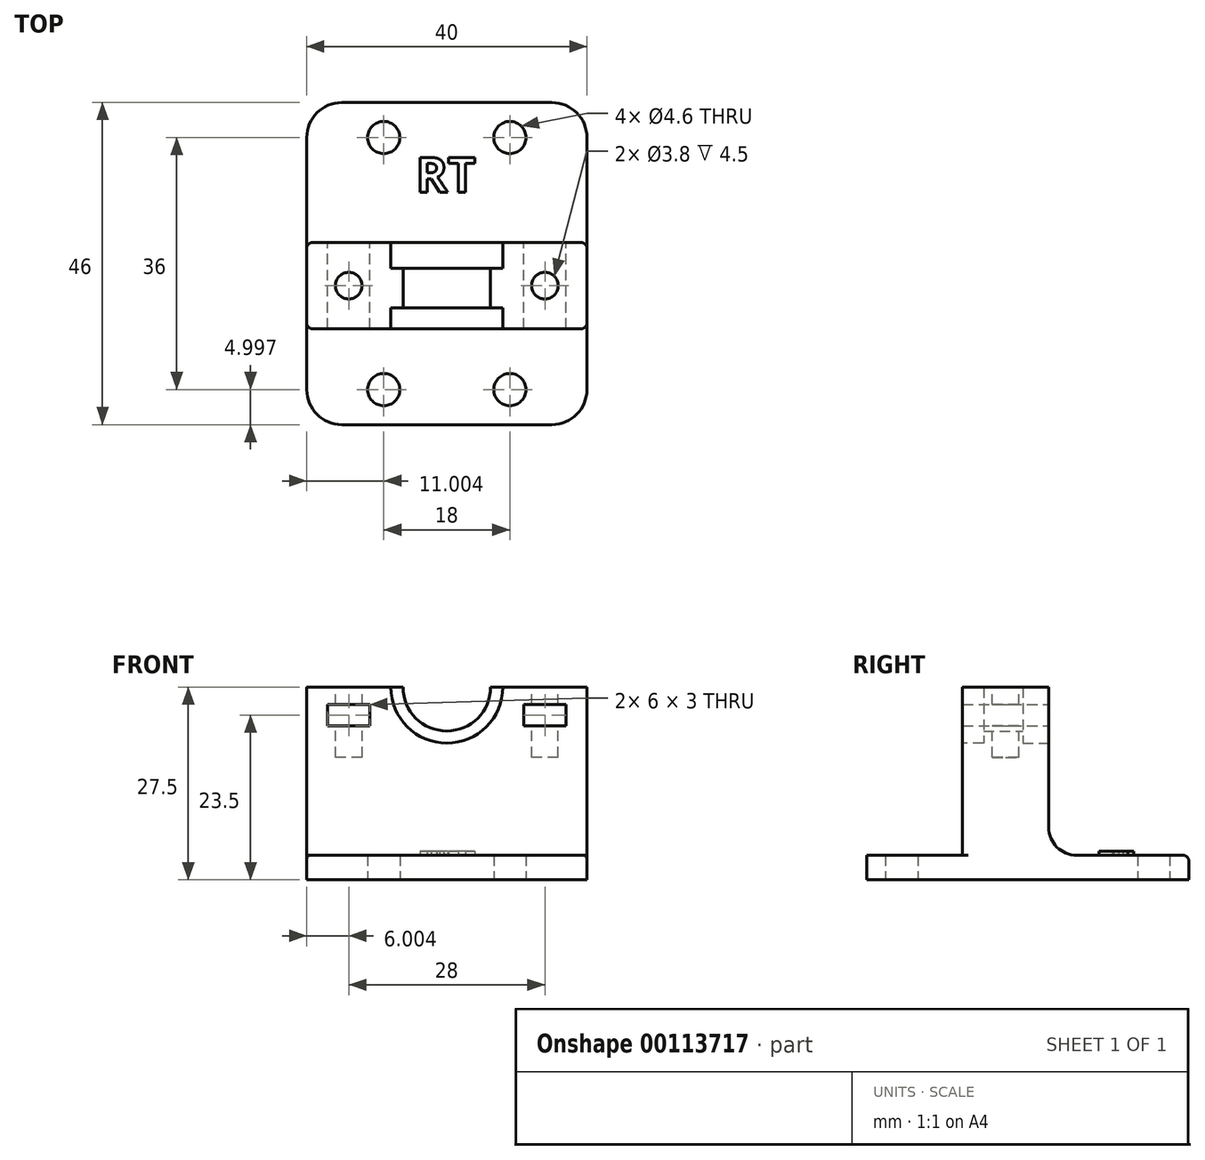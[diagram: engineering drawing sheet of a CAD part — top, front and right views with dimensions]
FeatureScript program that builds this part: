
annotation { "Feature Type Name" : "Feature", "Feature Type Description" : "" }
export const myFeature = defineFeature(function(context is Context, id is Id, definition is map)
    precondition{}
    {
        {
            var Q0;
            Q0=qCreatedBy(makeId("Top.planeOp"),FACE);
            var sketch = newSketch(context, id + "F0", { "sketchPlane" : qUnion([Q0])});
            skLineSegment(sketch, "E0.bottom", {"start": v(-24.7, 19.54) * mm, "end": v(15.3, 19.54) * mm});
            skLineSegment(sketch, "E0.top", {"start": v(-24.7, -26.46) * mm, "end": v(15.3, -26.46) * mm});
            skLineSegment(sketch, "E0.left", {"start": v(-24.7, 19.54) * mm, "end": v(-24.7, -26.46) * mm});
            skLineSegment(sketch, "E0.right", {"start": v(15.3, 19.54) * mm, "end": v(15.3, -26.46) * mm});
            skCircle(sketch, "E1", {"center": v(-13.7, 14.54) * mm, "radius": 2.3 * mm});
            skCircle(sketch, "E2.0.1.0", {"center": v(-13.7, -21.46) * mm, "radius": 2.3 * mm});
            skCircle(sketch, "E2.1.0.0", {"center": v(4.3, 14.54) * mm, "radius": 2.3 * mm});
            skCircle(sketch, "E2.1.1.0", {"center": v(4.3, -21.46) * mm, "radius": 2.3 * mm});
            skLineSegment(sketch, "E2.direction1", {"start": v(-13.7, 14.54) * mm, "end": v(4.3, 14.54) * mm, "construction": true});
            skLineSegment(sketch, "E2.direction2", {"start": v(-13.7, 14.54) * mm, "end": v(-13.7, -21.46) * mm, "construction": true});
            skSolve(sketch);
        }
        {
            var Q0;
            Q0=makeQuery(id+"F0.imprint","IMPRINT",FACE,{"disambiguationData":[TD([[makeQuery(id+"F0.imprint","IMPRINT",EDGE,{"derivedFrom":sQuery(id+"F0.wireOp",EDGE,"E0.bottom")}),-1.0]])]});
            extrude(context, id + "F1", {"entities" : qUnion([Q0]), "depth" : 3.5 * mm});
        }
        {
            var Q0;
            Q0=makeQuery(id+"F1.opExtrude","CAP_FACE",FACE,{"disambiguationData":[OSD([sQuery(id+"F0.wireOp",EDGE,"E0.bottom"),sQuery(id+"F0.wireOp",EDGE,"E0.top"),sQuery(id+"F0.wireOp",EDGE,"E0.left"),sQuery(id+"F0.wireOp",EDGE,"E0.right"),sQuery(id+"F0.wireOp",EDGE,"E1"),sQuery(id+"F0.wireOp",EDGE,"E2.0.1.0"),sQuery(id+"F0.wireOp",EDGE,"E2.1.0.0"),sQuery(id+"F0.wireOp",EDGE,"E2.1.1.0")])],"isStart":false});
            var sketch = newSketch(context, id + "F2", { "sketchPlane" : qUnion([Q0])});
            skLineSegment(sketch, "E3.bottom", {"start": v(-24.7, -0.46) * mm, "end": v(15.3, -0.46) * mm});
            skLineSegment(sketch, "E3.top", {"start": v(-24.7, -12.76) * mm, "end": v(15.3, -12.76) * mm});
            skLineSegment(sketch, "E3.left", {"start": v(-24.7, -0.46) * mm, "end": v(-24.7, -12.76) * mm});
            skLineSegment(sketch, "E3.right", {"start": v(15.3, -0.46) * mm, "end": v(15.3, -12.76) * mm});
            skSolve(sketch);
        }
        {
            var Q0;
            Q0=makeQuery(id+"F2.imprint","IMPRINT",FACE,{"disambiguationData":[TD([[makeQuery(id+"F2.imprint","IMPRINT",EDGE,{"derivedFrom":sQuery(id+"F2.wireOp",EDGE,"E3.bottom")}),-1.0]])]});
            extrude(context, id + "F3", {"entities" : qUnion([Q0]), "operationType" : NewBodyOperationType.ADD, "depth" : 24 * mm});
        }
        {
            var Q0;
            Q0=makeQuery(id+"F3.opExtrude","CAP_EDGE",EDGE,{"disambiguationData":[OSD([sQuery(id+"F2.wireOp",EDGE,"E3.top")])],"isStart":true});
            var Q1;
            Q1=makeQuery(id+"F3.opExtrude","CAP_EDGE",EDGE,{"disambiguationData":[OSD([sQuery(id+"F2.wireOp",EDGE,"E3.bottom")])],"isStart":true});
            fillet(context, id + "F4", {"entities" : qUnion([Q0, Q1]), "radius" : 4 * mm, "tangentPropagation" : true, "allowEdgeOverflow" : false});
        }
        {
            var Q0;
            Q0=makeQuery(id+"F3.opExtrude","SWEPT_FACE",FACE,{"disambiguationData":[OSD([sQuery(id+"F2.wireOp",EDGE,"E3.bottom")])]});
            var sketch = newSketch(context, id + "F5", { "sketchPlane" : qUnion([Q0])});
            skCircle(sketch, "E4", {"center": v(4.7, 27.5) * mm, "radius": 6.25 * mm});
            skSolve(sketch);
        }
        {
            var Q0;
            {var subQ0=sQuery(id+"F5.wireOp",EDGE,"E4");var subQ1=makeQuery(id+"F3.opExtrude","CAP_EDGE",EDGE,{"disambiguationData":[OSD([sQuery(id+"F2.wireOp",EDGE,"E3.bottom")])],"isStart":false});var subQ2=makeQuery(id+"F5.imprint","INTERSECT",VERTEX,{"disambiguationData":[OD(0.0)],"derivedFrom":[subQ1,subQ0]});Q0=makeQuery(id+"F5.imprint","IMPRINT",FACE,{"disambiguationData":[TD([[makeQuery(id+"F5.imprint","IMPRINT",EDGE,{"disambiguationData":[TD([[subQ2,1.0]])],"derivedFrom":subQ0}),1.0]])]});}
            extrude(context, id + "F6", {"entities" : qUnion([Q0]), "operationType" : NewBodyOperationType.REMOVE, "oppositeDirection" : true, "depth" : 25 * mm});
        }
        {
            var Q0;
            Q0=makeQuery(id+"F1.opExtrude","SWEPT_EDGE",EDGE,{"disambiguationData":[OSD([sQuery(id+"F0.wireOp",EDGE,"E0.bottom"),sQuery(id+"F0.wireOp",EDGE,"E0.right")])]});
            var Q1;
            Q1=makeQuery(id+"F1.opExtrude","SWEPT_EDGE",EDGE,{"disambiguationData":[OSD([sQuery(id+"F0.wireOp",EDGE,"E0.bottom"),sQuery(id+"F0.wireOp",EDGE,"E0.left")])]});
            var Q2;
            Q2=makeQuery(id+"F1.opExtrude","SWEPT_EDGE",EDGE,{"disambiguationData":[OSD([sQuery(id+"F0.wireOp",EDGE,"E0.top"),sQuery(id+"F0.wireOp",EDGE,"E0.right")])]});
            var Q3;
            Q3=makeQuery(id+"F1.opExtrude","SWEPT_EDGE",EDGE,{"disambiguationData":[OSD([sQuery(id+"F0.wireOp",EDGE,"E0.top"),sQuery(id+"F0.wireOp",EDGE,"E0.left")])]});
            fillet(context, id + "F7", {"entities" : qUnion([Q0, Q1, Q2, Q3]), "radius" : 5 * mm, "tangentPropagation" : true, "allowEdgeOverflow" : false});
        }
        {
            var Q0;
            {var subQ0=sQuery(id+"F2.wireOp",EDGE,"E3.top");var subQ1=sQuery(id+"F2.wireOp",EDGE,"E3.bottom");var subQ2=sQuery(id+"F2.wireOp",EDGE,"E3.right");Q0=makeQuery(id+"F6.boolean.opBoolean","SPLIT",FACE,{"disambiguationData":[TD([makeQuery(id+"F1.opExtrude","SWEPT_FACE",FACE,{"disambiguationData":[OSD([sQuery(id+"F0.wireOp",EDGE,"E0.right")])]})])],"derivedFrom":makeQuery(id+"F3.opExtrude","CAP_FACE",FACE,{"disambiguationData":[OSD([subQ1,subQ0,sQuery(id+"F2.wireOp",EDGE,"E3.left"),subQ2])],"isStart":false})});}
            var sketch = newSketch(context, id + "F8", { "sketchPlane" : qUnion([Q0])});
            skCircle(sketch, "E5", {"center": v(-18.7, -6.61) * mm, "radius": 1.9 * mm});
            skCircle(sketch, "E6.1.0.0", {"center": v(9.3, -6.61) * mm, "radius": 1.9 * mm});
            skLineSegment(sketch, "E6.direction1", {"start": v(-18.7, -6.61) * mm, "end": v(9.3, -6.61) * mm, "construction": true});
            skSolve(sketch);
        }
        {
            var Q0;
            Q0=makeQuery(id+"F8.imprint","IMPRINT",FACE,{"disambiguationData":[TD([[makeQuery(id+"F8.imprint","IMPRINT",EDGE,{"derivedFrom":sQuery(id+"F8.wireOp",EDGE,"E5")}),1.0]])]});
            var Q1;
            Q1=makeQuery(id+"F8.imprint","IMPRINT",FACE,{"disambiguationData":[TD([[makeQuery(id+"F8.imprint","IMPRINT",EDGE,{"derivedFrom":sQuery(id+"F8.wireOp",EDGE,"E6.1.0.0")}),1.0]])]});
            extrude(context, id + "F9", {"entities" : qUnion([Q0, Q1]), "operationType" : NewBodyOperationType.REMOVE, "oppositeDirection" : true, "depth" : 10 * mm});
        }
        {
            var Q0;
            Q0=makeQuery(id+"F3.opExtrude","SWEPT_FACE",FACE,{"disambiguationData":[OSD([sQuery(id+"F2.wireOp",EDGE,"E3.bottom")])]});
            var sketch = newSketch(context, id + "F10", { "sketchPlane" : qUnion([Q0])});
            skLineSegment(sketch, "E7.bottom", {"start": v(21.7, 22) * mm, "end": v(15.7, 22) * mm});
            skLineSegment(sketch, "E7.top", {"start": v(21.7, 25) * mm, "end": v(15.7, 25) * mm});
            skLineSegment(sketch, "E7.left", {"start": v(21.7, 22) * mm, "end": v(21.7, 25) * mm});
            skLineSegment(sketch, "E7.right", {"start": v(15.7, 22) * mm, "end": v(15.7, 25) * mm});
            skLineSegment(sketch, "E8.1.0.0", {"start": v(-6.3, 22) * mm, "end": v(-6.3, 25) * mm});
            skLineSegment(sketch, "E8.1.0.1", {"start": v(-6.3, 22) * mm, "end": v(-12.3, 22) * mm});
            skLineSegment(sketch, "E8.1.0.2", {"start": v(-6.3, 25) * mm, "end": v(-12.3, 25) * mm});
            skLineSegment(sketch, "E8.1.0.3", {"start": v(-12.3, 22) * mm, "end": v(-12.3, 25) * mm});
            skLineSegment(sketch, "E8.direction1", {"start": v(21.7, 22) * mm, "end": v(-6.3, 22) * mm, "construction": true});
            skSolve(sketch);
        }
        {
            var Q0;
            Q0=makeQuery(id+"F10.imprint","IMPRINT",FACE,{"disambiguationData":[TD([[makeQuery(id+"F10.imprint","IMPRINT",EDGE,{"derivedFrom":sQuery(id+"F10.wireOp",EDGE,"E7.bottom")}),-1.0]])]});
            var Q1;
            Q1=makeQuery(id+"F10.imprint","IMPRINT",FACE,{"disambiguationData":[TD([[makeQuery(id+"F10.imprint","IMPRINT",EDGE,{"derivedFrom":sQuery(id+"F10.wireOp",EDGE,"E8.1.0.0")}),1.0]])]});
            extrude(context, id + "F11", {"entities" : qUnion([Q0, Q1]), "operationType" : NewBodyOperationType.REMOVE, "oppositeDirection" : true, "depth" : 25 * mm});
        }
        {
            var Q0;
            Q0=makeQuery(id+"F3.opExtrude","SWEPT_FACE",FACE,{"disambiguationData":[OSD([sQuery(id+"F2.wireOp",EDGE,"E3.top")])]});
            var sketch = newSketch(context, id + "F12", { "sketchPlane" : qUnion([Q0])});
            skCircle(sketch, "E9", {"center": v(-4.7, 27.5) * mm, "radius": 8 * mm});
            skSolve(sketch);
        }
        {
            var Q0;
            {var subQ1=sQuery(id+"F2.wireOp",EDGE,"E3.top");var subQ2=makeQuery(id+"F3.opExtrude","SWEPT_FACE",FACE,{"disambiguationData":[OSD([subQ1])]});var subQ6=makeQuery(id+"F6.opExtrude","SWEPT_FACE",FACE,{"disambiguationData":[OSD([sQuery(id+"F5.wireOp",EDGE,"E4")])]});var subQ12=makeQuery(id+"F6.boolean.opBoolean","INTERSECT",EDGE,{"derivedFrom":[subQ2,subQ6]});Q0=makeQuery(id+"F12.imprint","IMPRINT",FACE,{"disambiguationData":[TD([[makeQuery(id+"F12.imprint","IMPRINT",EDGE,{"derivedFrom":subQ12}),1.0]])]});}
            extrude(context, id + "F13", {"entities" : qUnion([Q0]), "operationType" : NewBodyOperationType.REMOVE, "oppositeDirection" : true, "depth" : 3 * mm});
        }
        {
            var Q0;
            {var subQ0=sQuery(id+"F2.wireOp",EDGE,"E3.bottom");Q0=makeQuery(id+"F5.imprint","IMPRINT",FACE,{"disambiguationData":[TD([[makeQuery(id+"F5.imprint","IMPRINT",EDGE,{"derivedFrom":makeQuery(id+"F4.opFillet","BLEND_EDGE",EDGE,{"blendedFrom":[makeQuery(id+"F3.opExtrude","CAP_EDGE",EDGE,{"disambiguationData":[OSD([subQ0])],"isStart":true}),makeQuery(id+"F3.opExtrude","SWEPT_FACE",FACE,{"disambiguationData":[OSD([subQ0])]})],"blendedInto":[makeQuery(id+"F3.opExtrude","SWEPT_FACE",FACE,{"disambiguationData":[OSD([subQ0])]})]})}),1.0]])]});}
            var sketch = newSketch(context, id + "F14", { "sketchPlane" : qUnion([Q0])});
            skCircle(sketch, "E10", {"center": v(4.7, 27.5) * mm, "radius": 8 * mm});
            skSolve(sketch);
        }
        {
            var Q0;
            {var subQ1=sQuery(id+"F2.wireOp",EDGE,"E3.bottom");var subQ2=makeQuery(id+"F3.opExtrude","CAP_EDGE",EDGE,{"disambiguationData":[OSD([subQ1])],"isStart":false});var subQ3=sQuery(id+"F5.wireOp",EDGE,"E4");var subQ4=makeQuery(id+"F5.imprint","INTERSECT",VERTEX,{"disambiguationData":[OD(0.0)],"derivedFrom":[subQ2,subQ3]});var subQ10=makeQuery(id+"F5.imprint","IMPRINT",EDGE,{"disambiguationData":[TD([[subQ4,1.0]])],"derivedFrom":subQ3});Q0=makeQuery(id+"F14.imprint","IMPRINT",FACE,{"disambiguationData":[TD([[makeQuery(id+"F14.imprint","IMPRINT",EDGE,{"derivedFrom":subQ10}),-1.0]])]});}
            extrude(context, id + "F15", {"entities" : qUnion([Q0]), "operationType" : NewBodyOperationType.REMOVE, "oppositeDirection" : true, "depth" : 3.7 * mm});
        }
        {
            var Q0;
            Q0=makeQuery(id+"F3.opExtrude","SWEPT_EDGE",EDGE,{"disambiguationData":[OSD([sQuery(id+"F0.wireOp",EDGE,"E0.left"),sQuery(id+"F2.wireOp",EDGE,"E3.top"),sQuery(id+"F2.wireOp",EDGE,"E3.left")])]});
            var Q1;
            Q1=makeQuery(id+"F3.opExtrude","SWEPT_EDGE",EDGE,{"disambiguationData":[OSD([sQuery(id+"F0.wireOp",EDGE,"E0.right"),sQuery(id+"F2.wireOp",EDGE,"E3.top"),sQuery(id+"F2.wireOp",EDGE,"E3.right")])]});
            var Q2;
            Q2=makeQuery(id+"F3.opExtrude","SWEPT_EDGE",EDGE,{"disambiguationData":[OSD([sQuery(id+"F0.wireOp",EDGE,"E0.right"),sQuery(id+"F2.wireOp",EDGE,"E3.bottom"),sQuery(id+"F2.wireOp",EDGE,"E3.right")])]});
            var Q3;
            Q3=makeQuery(id+"F3.opExtrude","SWEPT_EDGE",EDGE,{"disambiguationData":[OSD([sQuery(id+"F0.wireOp",EDGE,"E0.left"),sQuery(id+"F2.wireOp",EDGE,"E3.bottom"),sQuery(id+"F2.wireOp",EDGE,"E3.left")])]});
            fillet(context, id + "F16", {"entities" : qUnion([Q0, Q1, Q2, Q3]), "radius" : 0.8 * mm, "tangentPropagation" : true, "allowEdgeOverflow" : false});
        }
        {
            var Q0;
            {var subQ0=sQuery(id+"F0.wireOp",EDGE,"E1");var subQ1=sQuery(id+"F0.wireOp",EDGE,"E0.right");var subQ2=sQuery(id+"F0.wireOp",EDGE,"E0.left");var subQ3=sQuery(id+"F0.wireOp",EDGE,"E0.bottom");var subQ4=sQuery(id+"F0.wireOp",EDGE,"E2.1.0.0");Q0=makeQuery(id+"F3.boolean.opBoolean","SPLIT",FACE,{"disambiguationData":[TD([makeQuery(id+"F1.opExtrude","SWEPT_FACE",FACE,{"disambiguationData":[OSD([subQ3])]})])],"derivedFrom":makeQuery(id+"F1.opExtrude","CAP_FACE",FACE,{"disambiguationData":[OSD([subQ3,sQuery(id+"F0.wireOp",EDGE,"E0.top"),subQ2,subQ1,subQ0,sQuery(id+"F0.wireOp",EDGE,"E2.0.1.0"),subQ4,sQuery(id+"F0.wireOp",EDGE,"E2.1.1.0")])],"isStart":false})});}
            var sketch = newSketch(context, id + "F17", { "sketchPlane" : qUnion([Q0])});
            skText(sketch, "E11", { "text": "RT", "fontName": "OpenSans-Bold.ttf"});
            skLineSegment(sketch, "E12", {"start": v(-4.7, 18.74) * mm, "end": v(-4.7, 1.58) * mm, "construction": true});
            const initialGuessF17  = {"E11": [-0.00916, 0.00674, 1, 0, 0.005]};
            skSetInitialGuess(sketch, initialGuessF17);
            skSolve(sketch);
        }
        {
            var Q0;
            Q0 = qSketchRegion(id + "F17", true);
            extrude(context, id + "F18", {"entities" : qUnion([Q0]), "operationType" : NewBodyOperationType.ADD, "depth" : 0.6 * mm});
        }
    });
